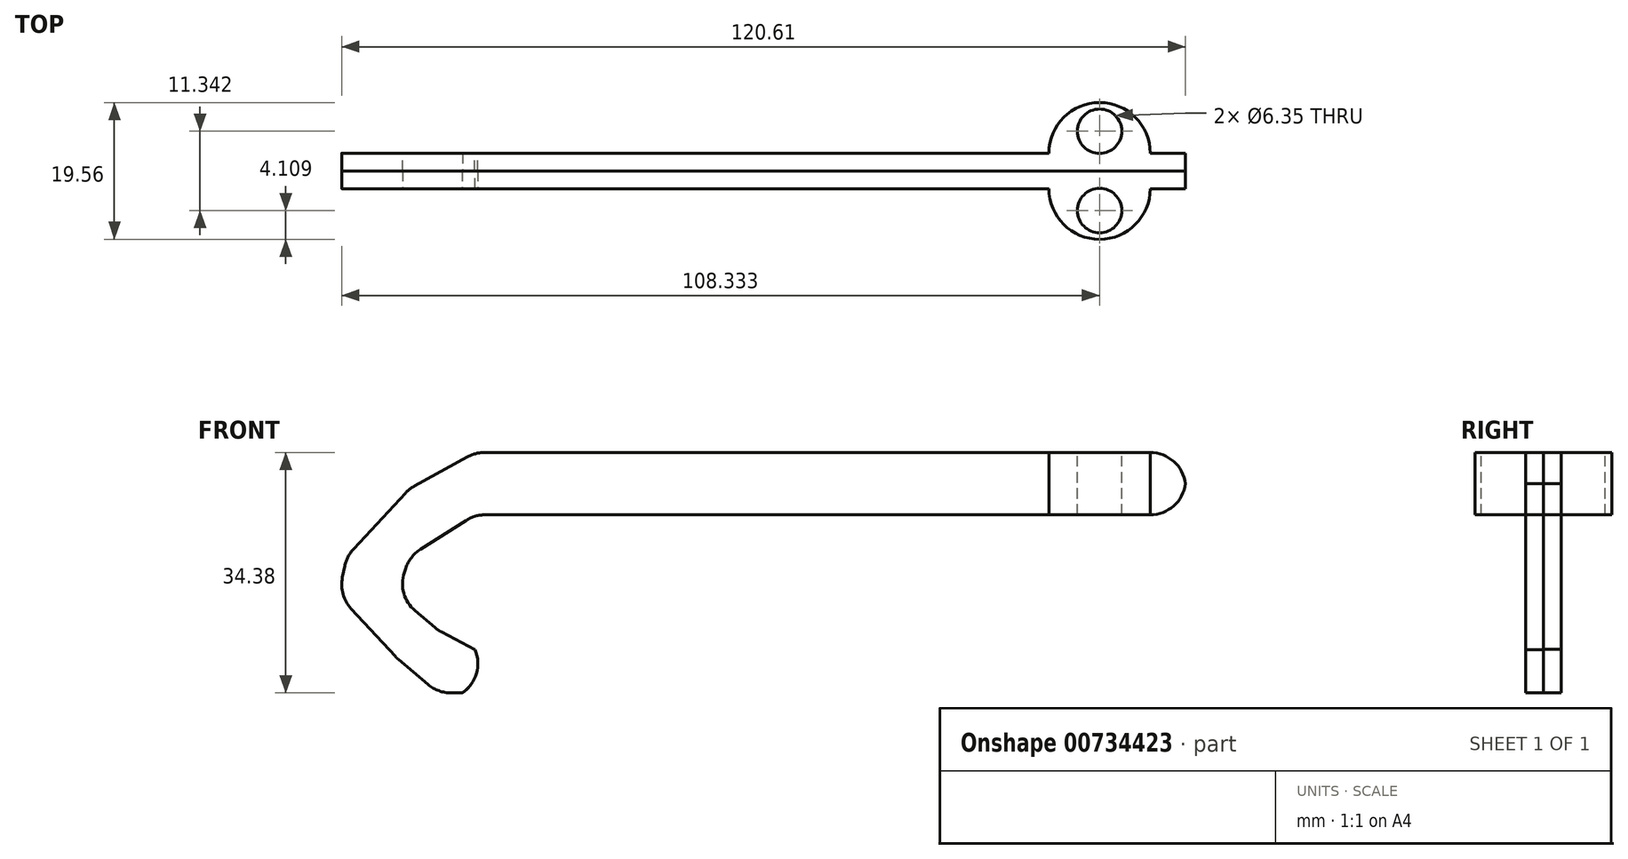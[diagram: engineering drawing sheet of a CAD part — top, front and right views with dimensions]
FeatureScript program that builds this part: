
annotation { "Feature Type Name" : "Feature", "Feature Type Description" : "" }
export const myFeature = defineFeature(function(context is Context, id is Id, definition is map)
    precondition{}
    {
        {
            var Q0;
            Q0=qCreatedBy(makeId("Front.planeOp"),FACE);
            var sketch = newSketch(context, id + "F0", { "sketchPlane" : qUnion([Q0])});
            skLineSegment(sketch, "E0", {"start": v(66.87, 23.27) * mm, "end": v(-34.73, 23.27) * mm});
            skLineSegment(sketch, "E1", {"start": v(66.87, 14.38) * mm, "end": v(-34.73, 14.38) * mm});
            skLineSegment(sketch, "E2", {"start": v(66.87, 23.27) * mm, "end": v(66.87, 14.38) * mm});
            skLineSegment(sketch, "E3", {"start": v(-34.73, 23.27) * mm, "end": v(-44.07, 18.1) * mm});
            skLineSegment(sketch, "E4", {"start": v(-34.73, 14.38) * mm, "end": v(-44.07, 8.44) * mm});
            skLineSegment(sketch, "E5", {"start": v(-44.07, 8.44) * mm, "end": v(-45.9, 2.85) * mm});
            skLineSegment(sketch, "E6", {"start": v(-45.9, 2.85) * mm, "end": v(-40, -2.14) * mm});
            skLineSegment(sketch, "E7", {"start": v(-40, -2.14) * mm, "end": v(-34.73, -4.9) * mm});
            skLineSegment(sketch, "E8", {"start": v(-34.73, -4.9) * mm, "end": v(-32.48, -8.75) * mm});
            skLineSegment(sketch, "E9", {"start": v(-32.48, -8.75) * mm, "end": v(-36.51, -11.1) * mm});
            skLineSegment(sketch, "E10", {"start": v(-36.51, -11.1) * mm, "end": v(-40, -11.1) * mm});
            skLineSegment(sketch, "E11", {"start": v(-40, -11.1) * mm, "end": v(-45.9, -6.12) * mm});
            skLineSegment(sketch, "E12", {"start": v(-45.9, -6.12) * mm, "end": v(-54.2, 2.85) * mm});
            skLineSegment(sketch, "E13", {"start": v(-54.2, 2.85) * mm, "end": v(-53.05, 8.44) * mm});
            skLineSegment(sketch, "E14", {"start": v(-53.05, 8.44) * mm, "end": v(-44.07, 18.1) * mm});
            skSolve(sketch);
        }
        {
            var Q0;
            Q0=makeQuery(id+"F0.imprint","IMPRINT",FACE,{"disambiguationData":[TD([[makeQuery(id+"F0.imprint","IMPRINT",EDGE,{"derivedFrom":sQuery(id+"F0.wireOp",EDGE,"E0")}),1.0]])]});
            extrude(context, id + "F1", {"entities" : qUnion([Q0]), "depth" : 2.54 * mm, "offsetDistance" : 25.4 * mm});
        }
        {
            var Q0;
            Q0=makeQuery(id+"F1.opExtrude","SWEPT_EDGE",EDGE,{"disambiguationData":[OSD([sQuery(id+"F0.wireOp",EDGE,"FaF548Dy-AH1d-7cey-Sdb6-neEY5Lz0bkhc"),sQuery(id+"F0.wireOp",EDGE,"2duHPpKX-Mklg-CAea-HiZF-ubxuLwDB73vv")])]});
            var Q1;
            Q1=makeQuery(id+"F1.opExtrude","SWEPT_EDGE",EDGE,{"disambiguationData":[OSD([sQuery(id+"F0.wireOp",EDGE,"2duHPpKX-Mklg-CAea-HiZF-ubxuLwDB73vv"),sQuery(id+"F0.wireOp",EDGE,"vMsXcqGC-UmtZ-yk9l-OPx9-qMXc5BvmLfo4")])]});
            var Q2;
            Q2=makeQuery(id+"F1.opExtrude","SWEPT_EDGE",EDGE,{"disambiguationData":[OSD([sQuery(id+"F0.wireOp",EDGE,"vMsXcqGC-UmtZ-yk9l-OPx9-qMXc5BvmLfo4"),sQuery(id+"F0.wireOp",EDGE,"a5tz0nlV-EvXU-qeEe-qzc3-pVyh4BvNrzzH")])]});
            var Q3;
            Q3=makeQuery(id+"F1.opExtrude","SWEPT_EDGE",EDGE,{"disambiguationData":[OSD([sQuery(id+"F0.wireOp",EDGE,"5MScrel3-bw4k-TXd2-RPPB-ftIyLXX6CxkY"),sQuery(id+"F0.wireOp",EDGE,"g0aZSll9-hpvP-WuqT-njGD-g9WgLA75pcPV")])]});
            var Q4;
            Q4=makeQuery(id+"F1.opExtrude","SWEPT_EDGE",EDGE,{"disambiguationData":[OSD([sQuery(id+"F0.wireOp",EDGE,"AhsYvQAR-oxIP-t0Il-eRO6-z4tD2zorvXqd"),sQuery(id+"F0.wireOp",EDGE,"5MScrel3-bw4k-TXd2-RPPB-ftIyLXX6CxkY")])]});
            var Q5;
            Q5=makeQuery(id+"F1.opExtrude","SWEPT_EDGE",EDGE,{"disambiguationData":[OSD([sQuery(id+"F0.wireOp",EDGE,"E1"),sQuery(id+"F0.wireOp",EDGE,"AhsYvQAR-oxIP-t0Il-eRO6-z4tD2zorvXqd")])]});
            var Q6;
            Q6=makeQuery(id+"F1.opExtrude","SWEPT_EDGE",EDGE,{"disambiguationData":[OSD([sQuery(id+"F0.wireOp",EDGE,"VicguIYn-3ePI-fVvz-yYVa-kae0SrEAnA5f"),sQuery(id+"F0.wireOp",EDGE,"FaF548Dy-AH1d-7cey-Sdb6-neEY5Lz0bkhc")])]});
            var Q7;
            Q7=makeQuery(id+"F1.opExtrude","SWEPT_EDGE",EDGE,{"disambiguationData":[OSD([sQuery(id+"F0.wireOp",EDGE,"E0"),sQuery(id+"F0.wireOp",EDGE,"a5tz0nlV-EvXU-qeEe-qzc3-pVyh4BvNrzzH")])]});
            fillet(context, id + "F2", {"entities" : qUnion([Q0, Q1, Q2, Q3, Q4, Q5, Q6, Q7]), "radius" : 5.08 * mm, "tangentPropagation" : true, "allowEdgeOverflow" : false});
        }
        {
            var Q0;
            Q0=makeQuery(id+"F1.opExtrude","SWEPT_FACE",FACE,{"disambiguationData":[OSD([sQuery(id+"F0.wireOp",EDGE,"E0")])]});
            var sketch = newSketch(context, id + "F3", { "sketchPlane" : qUnion([Q0])});
            skArc(sketch, "E15", {"start": v(47.31, -2.54) * mm, "mid": v(54.55, -9.78) * mm, "end": v(61.8, -2.54) * mm});
            skSolve(sketch);
        }
        {
            var Q0;
            {var subQ0=sQuery(id+"F3.wireOp",EDGE,"E15");Q0=makeQuery(id+"F3.imprint","IMPRINT",FACE,{"disambiguationData":[TD([[makeQuery(id+"F3.imprint","IMPRINT",EDGE,{"derivedFrom":subQ0}),1.0]])]});}
            var Q1;
            Q1=makeQuery(id+"F1.opExtrude","SWEPT_FACE",FACE,{"disambiguationData":[OSD([sQuery(id+"F0.wireOp",EDGE,"E1")])]});
            extrude(context, id + "F4", {"entities" : qUnion([Q0]), "operationType" : NewBodyOperationType.ADD, "endBound" : BoundingType.UP_TO_SURFACE, "oppositeDirection" : true, "depth" : 3.3 * mm, "endBoundEntityFace" : qUnion([Q1]), "offsetDistance" : 25.4 * mm});
        }
        {
            var Q0;
            {var subQ0=sQuery(id+"F0.wireOp",EDGE,"E0");Q0=makeQuery(id+"F4.boolean.opBoolean","MERGE",FACE,{"derivedFrom":[makeQuery(id+"F1.opExtrude","SWEPT_FACE",FACE,{"disambiguationData":[OSD([subQ0])]}),makeQuery(id+"F4.opExtrude","CAP_FACE",FACE,{"disambiguationData":[OSD([subQ0,sQuery(id+"F3.wireOp",EDGE,"E15")])],"isStart":true})]});}
            var sketch = newSketch(context, id + "F5", { "sketchPlane" : qUnion([Q0])});
            skCircle(sketch, "E16", {"center": v(54.55, -5.67) * mm, "radius": 3.18 * mm});
            skPoint(sketch, "E16.centerSnap0", {"position": v(54.55, -9.78) * mm});
            skSolve(sketch);
        }
        {
            var Q0;
            Q0=makeQuery(id+"F5.imprint","IMPRINT",FACE,{"disambiguationData":[TD([[makeQuery(id+"F5.imprint","IMPRINT",EDGE,{"derivedFrom":sQuery(id+"F5.wireOp",EDGE,"E16")}),1.0]])]});
            extrude(context, id + "F6", {"entities" : qUnion([Q0]), "operationType" : NewBodyOperationType.REMOVE, "oppositeDirection" : true, "depth" : 25.4 * mm, "offsetDistance" : 25.4 * mm});
        }
        {
            var Q0;
            Q0=makeQuery(id+"F1.opExtrude","SWEPT_BODY",BODY,{"disambiguationData":[OSD([sQuery(id+"F0.wireOp",EDGE,"E0"),sQuery(id+"F0.wireOp",EDGE,"E1"),sQuery(id+"F0.wireOp",EDGE,"E2"),sQuery(id+"F0.wireOp",EDGE,"E3"),sQuery(id+"F0.wireOp",EDGE,"E4"),sQuery(id+"F0.wireOp",EDGE,"E5"),sQuery(id+"F0.wireOp",EDGE,"E6"),sQuery(id+"F0.wireOp",EDGE,"E7"),sQuery(id+"F0.wireOp",EDGE,"E8"),sQuery(id+"F0.wireOp",EDGE,"E9"),sQuery(id+"F0.wireOp",EDGE,"E10"),sQuery(id+"F0.wireOp",EDGE,"E11"),sQuery(id+"F0.wireOp",EDGE,"E12"),sQuery(id+"F0.wireOp",EDGE,"E13"),sQuery(id+"F0.wireOp",EDGE,"E14")])]});
            var Q1;
            Q1=qCreatedBy(makeId("Front.planeOp"),FACE);
            mirror(context, id + "F7", {"entities" : qUnion([Q0]), "mirrorPlane" : qUnion([Q1])});
        }
        {
            var Q0;
            Q0=makeQuery(id+"F7.opPattern","COPY",EDGE,{"derivedFrom":makeQuery(id+"F1.opExtrude","SWEPT_EDGE",EDGE,{"disambiguationData":[OSD([sQuery(id+"F0.wireOp",EDGE,"E8"),sQuery(id+"F0.wireOp",EDGE,"E9")])]}),"instanceName":"1"});
            var Q1;
            Q1=makeQuery(id+"F1.opExtrude","SWEPT_EDGE",EDGE,{"disambiguationData":[OSD([sQuery(id+"F0.wireOp",EDGE,"E8"),sQuery(id+"F0.wireOp",EDGE,"E9")])]});
            var Q2;
            Q2=makeQuery(id+"F1.opExtrude","SWEPT_EDGE",EDGE,{"disambiguationData":[OSD([sQuery(id+"F0.wireOp",EDGE,"E10"),sQuery(id+"F0.wireOp",EDGE,"E11")])]});
            var Q3;
            Q3=makeQuery(id+"F7.opPattern","COPY",EDGE,{"derivedFrom":makeQuery(id+"F1.opExtrude","SWEPT_EDGE",EDGE,{"disambiguationData":[OSD([sQuery(id+"F0.wireOp",EDGE,"E10"),sQuery(id+"F0.wireOp",EDGE,"E11")])]}),"instanceName":"1"});
            var Q4;
            Q4=makeQuery(id+"F1.opExtrude","SWEPT_EDGE",EDGE,{"disambiguationData":[OSD([sQuery(id+"F0.wireOp",EDGE,"E6"),sQuery(id+"F0.wireOp",EDGE,"E7")])]});
            var Q5;
            Q5=makeQuery(id+"F7.opPattern","COPY",EDGE,{"derivedFrom":makeQuery(id+"F1.opExtrude","SWEPT_EDGE",EDGE,{"disambiguationData":[OSD([sQuery(id+"F0.wireOp",EDGE,"E6"),sQuery(id+"F0.wireOp",EDGE,"E7")])]}),"instanceName":"1"});
            var Q6;
            Q6=makeQuery(id+"F1.opExtrude","SWEPT_EDGE",EDGE,{"disambiguationData":[OSD([sQuery(id+"F0.wireOp",EDGE,"E5"),sQuery(id+"F0.wireOp",EDGE,"E6")])]});
            var Q7;
            Q7=makeQuery(id+"F7.opPattern","COPY",EDGE,{"derivedFrom":makeQuery(id+"F1.opExtrude","SWEPT_EDGE",EDGE,{"disambiguationData":[OSD([sQuery(id+"F0.wireOp",EDGE,"E5"),sQuery(id+"F0.wireOp",EDGE,"E6")])]}),"instanceName":"1"});
            var Q8;
            Q8=makeQuery(id+"F1.opExtrude","SWEPT_EDGE",EDGE,{"disambiguationData":[OSD([sQuery(id+"F0.wireOp",EDGE,"E4"),sQuery(id+"F0.wireOp",EDGE,"E5")])]});
            var Q9;
            Q9=makeQuery(id+"F7.opPattern","COPY",EDGE,{"derivedFrom":makeQuery(id+"F1.opExtrude","SWEPT_EDGE",EDGE,{"disambiguationData":[OSD([sQuery(id+"F0.wireOp",EDGE,"E4"),sQuery(id+"F0.wireOp",EDGE,"E5")])]}),"instanceName":"1"});
            var Q10;
            Q10=makeQuery(id+"F1.opExtrude","SWEPT_EDGE",EDGE,{"disambiguationData":[OSD([sQuery(id+"F0.wireOp",EDGE,"E13"),sQuery(id+"F0.wireOp",EDGE,"E14")])]});
            var Q11;
            Q11=makeQuery(id+"F1.opExtrude","SWEPT_EDGE",EDGE,{"disambiguationData":[OSD([sQuery(id+"F0.wireOp",EDGE,"E12"),sQuery(id+"F0.wireOp",EDGE,"E13")])]});
            var Q12;
            Q12=makeQuery(id+"F7.opPattern","COPY",EDGE,{"derivedFrom":makeQuery(id+"F1.opExtrude","SWEPT_EDGE",EDGE,{"disambiguationData":[OSD([sQuery(id+"F0.wireOp",EDGE,"E12"),sQuery(id+"F0.wireOp",EDGE,"E13")])]}),"instanceName":"1"});
            var Q13;
            Q13=makeQuery(id+"F7.opPattern","COPY",EDGE,{"derivedFrom":makeQuery(id+"F1.opExtrude","SWEPT_EDGE",EDGE,{"disambiguationData":[OSD([sQuery(id+"F0.wireOp",EDGE,"E13"),sQuery(id+"F0.wireOp",EDGE,"E14")])]}),"instanceName":"1"});
            var Q14;
            Q14=makeQuery(id+"F1.opExtrude","SWEPT_EDGE",EDGE,{"disambiguationData":[OSD([sQuery(id+"F0.wireOp",EDGE,"E11"),sQuery(id+"F0.wireOp",EDGE,"E12")])]});
            var Q15;
            Q15=makeQuery(id+"F7.opPattern","COPY",EDGE,{"derivedFrom":makeQuery(id+"F1.opExtrude","SWEPT_EDGE",EDGE,{"disambiguationData":[OSD([sQuery(id+"F0.wireOp",EDGE,"E11"),sQuery(id+"F0.wireOp",EDGE,"E12")])]}),"instanceName":"1"});
            var Q16;
            Q16=makeQuery(id+"F1.opExtrude","SWEPT_EDGE",EDGE,{"disambiguationData":[OSD([sQuery(id+"F0.wireOp",EDGE,"E3"),sQuery(id+"F0.wireOp",EDGE,"E14")])]});
            var Q17;
            Q17=makeQuery(id+"F7.opPattern","COPY",EDGE,{"derivedFrom":makeQuery(id+"F1.opExtrude","SWEPT_EDGE",EDGE,{"disambiguationData":[OSD([sQuery(id+"F0.wireOp",EDGE,"E3"),sQuery(id+"F0.wireOp",EDGE,"E14")])]}),"instanceName":"1"});
            fillet(context, id + "F8", {"entities" : qUnion([Q0, Q1, Q2, Q3, Q4, Q5, Q6, Q7, Q8, Q9, Q10, Q11, Q12, Q13, Q14, Q15, Q16, Q17]), "radius" : 5.08 * mm, "tangentPropagation" : true, "allowEdgeOverflow" : false});
        }
    });
